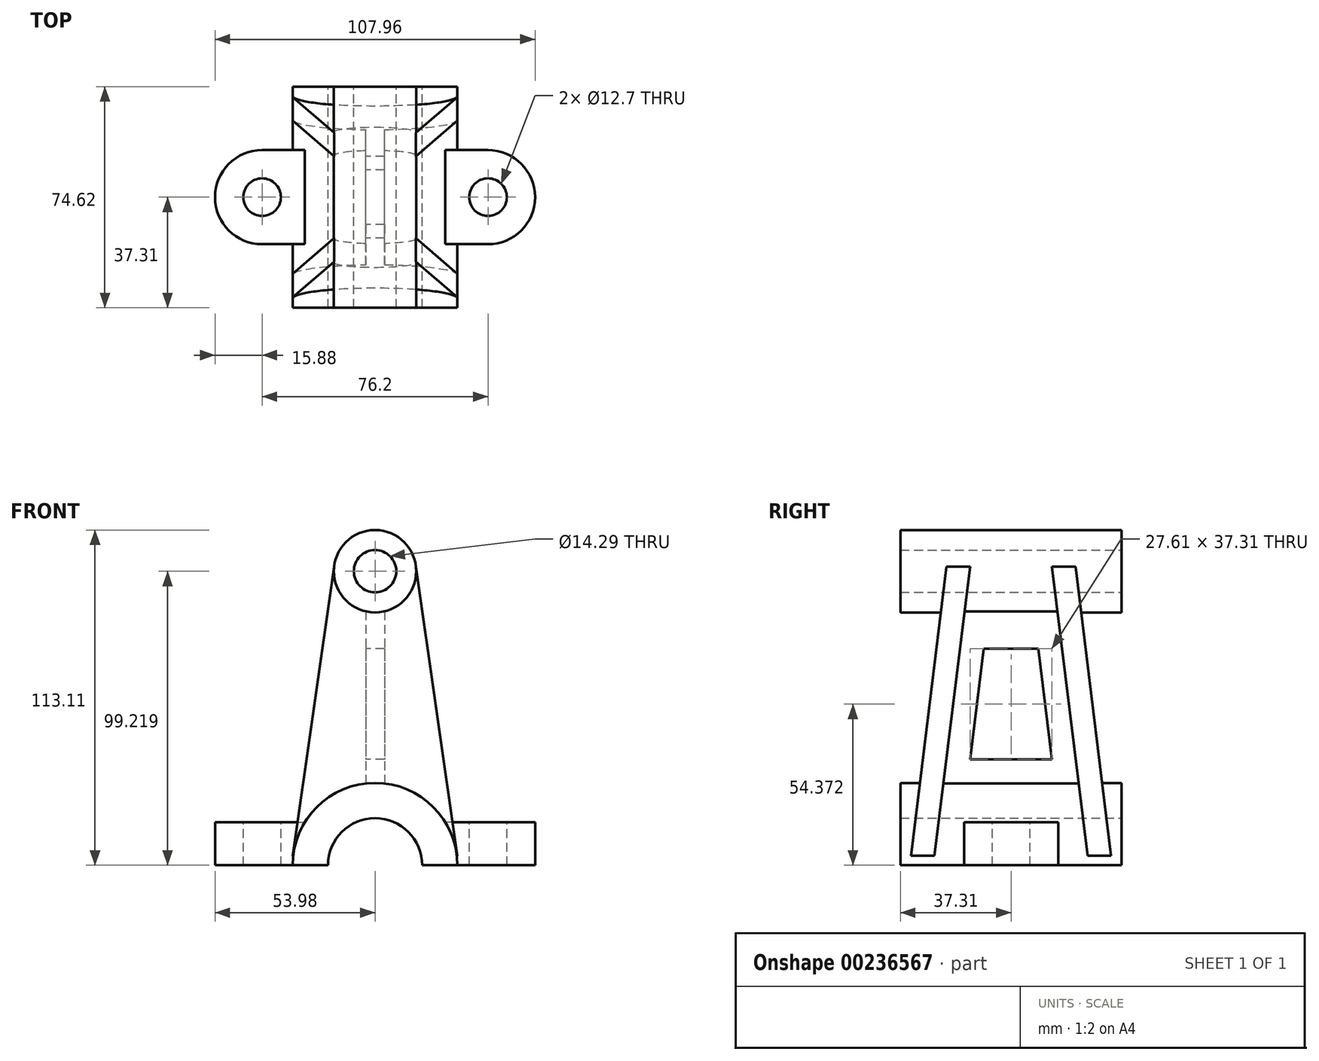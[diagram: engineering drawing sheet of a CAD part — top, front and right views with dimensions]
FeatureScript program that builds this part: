
annotation { "Feature Type Name" : "Feature", "Feature Type Description" : "" }
export const myFeature = defineFeature(function(context is Context, id is Id, definition is map)
    precondition{}
    {
        {
            var Q0;
            Q0=qCreatedBy(makeId("Front.planeOp"),FACE);
            var sketch = newSketch(context, id + "F0", { "sketchPlane" : qUnion([Q0])});
            skArc(sketch, "E0", {"start": v(27.78, 0) * mm, "mid": v(0, 27.78) * mm, "end": v(-27.78, 0) * mm});
            skPoint(sketch, "E1.orphan", {"position": v(-27.78, 0) * mm});
            skArc(sketch, "E2", {"start": v(15.88, 0) * mm, "mid": v(0, 15.88) * mm, "end": v(-15.88, 0) * mm});
            skLineSegment(sketch, "E3.trimOffspring", {"start": v(15.88, 0) * mm, "end": v(53.98, 0) * mm});
            skLineSegment(sketch, "E4", {"start": v(53.98, 0) * mm, "end": v(53.98, 14.57) * mm});
            skLineSegment(sketch, "E5", {"start": v(53.98, 14.57) * mm, "end": v(23.65, 14.57) * mm});
            skLineSegment(sketch, "E6.MirrorCS", {"start": v(-53.98, 14.57) * mm, "end": v(-23.65, 14.57) * mm});
            skLineSegment(sketch, "E7.MirrorCS", {"start": v(-53.98, 0) * mm, "end": v(-53.98, 14.57) * mm});
            skLineSegment(sketch, "E8.MirrorCS", {"start": v(-15.88, 0) * mm, "end": v(-53.98, 0) * mm});
            skCircle(sketch, "E9", {"center": v(0, 99.22) * mm, "radius": 13.9 * mm});
            skCircle(sketch, "E10", {"center": v(0, 99.22) * mm, "radius": 7.14 * mm});
            skLineSegment(sketch, "E11", {"start": v(-15.88, 0) * mm, "end": v(15.88, 0) * mm});
            skSolve(sketch);
        }
        {
            var Q0;
            {var subQ0=sQuery(id+"F0.wireOp",EDGE,"E2");Q0=makeQuery(id+"F0.imprint","IMPRINT",FACE,{"disambiguationData":[TD([[makeQuery(id+"F0.imprint","IMPRINT",EDGE,{"derivedFrom":subQ0}),-1.0]])]});}
            extrude(context, id + "F1", {"entities" : qUnion([Q0]), "endBound" : BoundingType.SYMMETRIC, "depth" : 74.61 * mm});
        }
        {
            var Q0;
            {var subQ4=sQuery(id+"F0.wireOp",EDGE,"E4");Q0=makeQuery(id+"F0.imprint","IMPRINT",FACE,{"disambiguationData":[TD([[makeQuery(id+"F0.imprint","IMPRINT",EDGE,{"derivedFrom":subQ4}),1.0]])]});}
            var Q1;
            {var subQ3=sQuery(id+"F0.wireOp",EDGE,"E6.MirrorCS");Q1=makeQuery(id+"F0.imprint","IMPRINT",FACE,{"disambiguationData":[TD([[makeQuery(id+"F0.imprint","IMPRINT",EDGE,{"derivedFrom":subQ3}),-1.0]])]});}
            extrude(context, id + "F2", {"entities" : qUnion([Q0, Q1]), "operationType" : NewBodyOperationType.ADD, "endBound" : BoundingType.SYMMETRIC, "depth" : 31.75 * mm});
        }
        {
            var Q0;
            Q0=makeQuery(id+"F2.opExtrude","CAP_EDGE",EDGE,{"disambiguationData":[OSD([sQuery(id+"F0.wireOp",EDGE,"E4")])],"isStart":false});
            var Q1;
            Q1=makeQuery(id+"F2.opExtrude","CAP_EDGE",EDGE,{"disambiguationData":[OSD([sQuery(id+"F0.wireOp",EDGE,"E4")])],"isStart":true});
            var Q2;
            Q2=makeQuery(id+"F2.opExtrude","CAP_EDGE",EDGE,{"disambiguationData":[OSD([sQuery(id+"F0.wireOp",EDGE,"E7.MirrorCS")])],"isStart":false});
            var Q3;
            Q3=makeQuery(id+"F2.opExtrude","CAP_EDGE",EDGE,{"disambiguationData":[OSD([sQuery(id+"F0.wireOp",EDGE,"E7.MirrorCS")])],"isStart":true});
            fillet(context, id + "F3", {"entities" : qUnion([Q0, Q1, Q2, Q3]), "radius" : 15.88 * mm, "tangentPropagation" : true, "allowEdgeOverflow" : false});
        }
        {
            var Q0;
            Q0=makeQuery(id+"F0.imprint","IMPRINT",FACE,{"disambiguationData":[TD([[makeQuery(id+"F0.imprint","IMPRINT",EDGE,{"derivedFrom":sQuery(id+"F0.wireOp",EDGE,"E9")}),1.0]])]});
            extrude(context, id + "F4", {"entities" : qUnion([Q0]), "endBound" : BoundingType.SYMMETRIC, "depth" : 74.61 * mm});
        }
        {
            var Q0;
            Q0=qCreatedBy(makeId("Right.planeOp"),FACE);
            var sketch = newSketch(context, id + "F5", { "sketchPlane" : qUnion([Q0])});
            skLineSegment(sketch, "E12", {"start": v(-33.73, 3.17) * mm, "end": v(-21.75, 100.8) * mm});
            skLineSegment(sketch, "E13", {"start": v(-21.75, 100.8) * mm, "end": v(-13.8, 100.8) * mm});
            skLineSegment(sketch, "E14", {"start": v(-13.8, 100.8) * mm, "end": v(-25.8, 3.18) * mm});
            skLineSegment(sketch, "E15", {"start": v(-25.8, 3.18) * mm, "end": v(-33.73, 3.18) * mm});
            skLineSegment(sketch, "E16.MirrorCS", {"start": v(13.8, 100.8) * mm, "end": v(25.8, 3.18) * mm});
            skLineSegment(sketch, "E17.MirrorCS", {"start": v(33.73, 3.17) * mm, "end": v(21.75, 100.8) * mm});
            skLineSegment(sketch, "E18.MirrorCS", {"start": v(25.8, 3.18) * mm, "end": v(33.73, 3.18) * mm});
            skLineSegment(sketch, "E19.MirrorCS", {"start": v(21.75, 100.8) * mm, "end": v(13.8, 100.8) * mm});
            skLineSegment(sketch, "E20.0", {"start": v(9.22, 73.03) * mm, "end": v(13.8, 35.72) * mm});
            skLineSegment(sketch, "E21.0", {"start": v(-9.22, 73.03) * mm, "end": v(-13.8, 35.72) * mm});
            skLineSegment(sketch, "E22", {"start": v(-13.8, 35.72) * mm, "end": v(13.8, 35.72) * mm});
            skLineSegment(sketch, "E23", {"start": v(-9.22, 73.03) * mm, "end": v(9.22, 73.03) * mm});
            skLineSegment(sketch, "E24", {"start": v(-15.2, 89.5) * mm, "end": v(15.2, 89.5) * mm});
            skLineSegment(sketch, "E25", {"start": v(-23.1, 25.12) * mm, "end": v(23.1, 25.12) * mm});
            skSolve(sketch);
        }
        {
            var Q0;
            Q0=makeQuery(id+"F5.imprint","IMPRINT",FACE,{"disambiguationData":[TD([[makeQuery(id+"F5.imprint","IMPRINT",EDGE,{"derivedFrom":sQuery(id+"F5.wireOp",EDGE,"E20.0")}),1.0]])]});
            extrude(context, id + "F6", {"entities" : qUnion([Q0]), "endBound" : BoundingType.SYMMETRIC, "depth" : 6.35 * mm});
        }
        {
            var Q0;
            Q0=makeQuery(id+"F5.imprint","IMPRINT",FACE,{"disambiguationData":[TD([[makeQuery(id+"F5.imprint","IMPRINT",EDGE,{"derivedFrom":sQuery(id+"F5.wireOp",EDGE,"E12")}),-1.0]])]});
            var Q1;
            Q1=makeQuery(id+"F5.imprint","IMPRINT",FACE,{"disambiguationData":[TD([[makeQuery(id+"F5.imprint","IMPRINT",EDGE,{"derivedFrom":sQuery(id+"F5.wireOp",EDGE,"E17.MirrorCS")}),1.0]])]});
            extrude(context, id + "F7", {"entities" : qUnion([Q0, Q1]), "operationType" : NewBodyOperationType.ADD, "endBound" : BoundingType.SYMMETRIC, "depth" : (1 + 3 / 32) * 50.8 * mm});
        }
        {
            var Q0;
            Q0=makeQuery(id+"F7.opExtrude","CAP_EDGE",EDGE,{"disambiguationData":[OSD([sQuery(id+"F5.wireOp",EDGE,"E19.MirrorCS")])],"isStart":false});
            var Q1;
            Q1=makeQuery(id+"F7.opExtrude","CAP_EDGE",EDGE,{"disambiguationData":[OSD([sQuery(id+"F5.wireOp",EDGE,"E13")])],"isStart":true});
            chamfer(context, id + "F8", {"entities" : qUnion([Q0, Q1]), "chamferType" : ChamferType.TWO_OFFSETS, "width1" : 13.98 * mm, "oppositeDirection" : true, "width2" : 97.63 * mm, "tangentPropagation" : true});
        }
        {
            var Q0;
            Q0=makeQuery(id+"F0.imprint","IMPRINT",FACE,{"disambiguationData":[TD([[makeQuery(id+"F0.imprint","IMPRINT",EDGE,{"derivedFrom":sQuery(id+"F0.wireOp",EDGE,"E2")}),1.0]])]});
            extrude(context, id + "F9", {"entities" : qUnion([Q0]), "operationType" : NewBodyOperationType.REMOVE, "endBound" : BoundingType.SYMMETRIC, "oppositeDirection" : true, "depth" : 101.6 * mm});
        }
        {
            var Q0;
            Q0=makeQuery(id+"F2.opExtrude","SWEPT_FACE",FACE,{"disambiguationData":[OSD([sQuery(id+"F0.wireOp",EDGE,"E5")])]});
            var sketch = newSketch(context, id + "F10", { "sketchPlane" : qUnion([Q0])});
            skCircle(sketch, "E26", {"center": v(-38.1, 0) * mm, "radius": 6.35 * mm});
            skCircle(sketch, "E27", {"center": v(38.1, 0) * mm, "radius": 6.35 * mm});
            skSolve(sketch);
        }
        {
            var Q0;
            Q0=makeQuery(id+"F10.imprint","IMPRINT",FACE,{"disambiguationData":[TD([[makeQuery(id+"F10.imprint","IMPRINT",EDGE,{"derivedFrom":sQuery(id+"F10.wireOp",EDGE,"E26")}),1.0]])]});
            var Q1;
            Q1=makeQuery(id+"F10.imprint","IMPRINT",FACE,{"disambiguationData":[TD([[makeQuery(id+"F10.imprint","IMPRINT",EDGE,{"derivedFrom":sQuery(id+"F10.wireOp",EDGE,"E27")}),1.0]])]});
            extrude(context, id + "F11", {"entities" : qUnion([Q0, Q1]), "operationType" : NewBodyOperationType.REMOVE, "endBound" : BoundingType.THROUGH_ALL, "oppositeDirection" : true, "depth" : 25.4 * mm});
        }
        {
            var Q0;
            Q0=makeQuery(id+"F0.imprint","IMPRINT",FACE,{"disambiguationData":[TD([[makeQuery(id+"F0.imprint","IMPRINT",EDGE,{"derivedFrom":sQuery(id+"F0.wireOp",EDGE,"E10")}),1.0]])]});
            extrude(context, id + "F12", {"entities" : qUnion([Q0]), "operationType" : NewBodyOperationType.REMOVE, "endBound" : BoundingType.SYMMETRIC, "oppositeDirection" : true, "depth" : 76.2 * mm});
        }
        {
            var Q0;
            Q0=makeQuery(id+"F7.opExtrude","CAP_EDGE",EDGE,{"disambiguationData":[OSD([sQuery(id+"F5.wireOp",EDGE,"E19.MirrorCS")])],"isStart":true});
            var Q1;
            Q1=makeQuery(id+"F7.opExtrude","CAP_EDGE",EDGE,{"disambiguationData":[OSD([sQuery(id+"F5.wireOp",EDGE,"E13")])],"isStart":false});
            chamfer(context, id + "F13", {"entities" : qUnion([Q0, Q1]), "chamferType" : ChamferType.TWO_OFFSETS, "width1" : 13.98 * mm, "oppositeDirection" : false, "width2" : 97.63 * mm, "tangentPropagation" : true});
        }
    });
